# Revit family: FP-Revit20-en-OS60SMTNB1-OS60SMTNG1-SteamOven-0-90003586A-AU-NZ-SG-IE-UK-CN
name_source: partatom
category: Specialty Equipment
units: mm (PartAtom-declared; Revit-internal decimal feet)

## family parameters
Always vertical = Yes
Cut with Voids When Loaded = Yes
OmniClass Number = 23.40.40.14.17.11
OmniClass Title = Cookers, Ovens, Stoves
Part Type = Normal
Room Calculation Point = No
Round Connector Dimension = Use Diameter
Shared = No
Work Plane-Based = No

## types (2) — shared parameters
Cavity - Depth = 550 mm
Cavity - Height = 580 mm
Cavity - Width = 560 mm
Chassis - Depth = 545 mm
Chassis - Height = 575 mm
Chassis - Width = 556 mm  [stored 1.82415 ft]
Connector Description - Electrical = 220-240V, 50Hz, 20A
Description = Combination Steam Oven, 60cm, 23 Function
Manufacturer = Fisher & Paykel Appliances
Material - Body = Fisher & Paykel - Grey
Material - Structure = Fisher & Paykel - Black
Material - Trim = Fisher & Paykel - Aluminium, Dark
Opening - Height = 487 mm
Product - Depth (Exc. Handles) = 565 mm  [stored 1.85367 ft]
Product - Height = 598 mm
Product - Width = 596 mm
URL = www.fisherpaykel.com
Visibility - Clearance Required = Yes
zero-valued in all types: Default Elevation

## per-type parameters (varying)
| type | Material - Glass | Model |
| OS60MTNB1 (Black Glass) | Fisher & Paykel - Glass, Black | OS60NMTNB1 |
| OS60SMTNG1 (Grey Glass) | Fisher & Paykel - Glass, Grey | OS60SMTNG1 |

note: [stored X ft] marks values corroborated as IEEE doubles in the binary element streams (Revit-internal decimal feet)

## geometry (parser evidence)
native form markers: Sweep x8
no freeform markers — native parametric forms only
